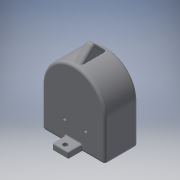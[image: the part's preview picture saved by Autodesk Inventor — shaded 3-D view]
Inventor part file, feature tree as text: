
AUTODESK INVENTOR PART (.ipt)
format: ipt  version: 2018 (Build 220112000, 112)  size: 283,648 bytes
history: native  units: in
note: dims shown in document units (in); Inventor stores cm internally (conversion verified against a paired STEP export)
features: extrude x7, fillet x7, sketch x6, reference x5, plane x1
ambient origin geometry x8: Origin, YZ Plane, XZ Plane, XY Plane, X Axis, Y Axis, Z Axis, Center Point
bodies: Solid1 (feature_tree)
feature tree (26):
  extrude  "Extrusion1"  Depth=0.197in
  extrude  "Extrusion2"  Depth=0.15in
  extrude  "Extrusion3"  Depth=0.4in TaperAngle=0.0deg
  extrude  "Extrusion4"  Depth=0.5in
  extrude  "Extrusion5"  Depth=0.4in TaperAngle=0.0deg
  plane  "Work Plane1"
  extrude  "Extrusion6"  Depth=0.1378in
  extrude  "Extrusion7"  Depth=0.4in TaperAngle=0.0deg
  fillet  "Fillet1"  Radius=0.5in
  fillet  "Fillet2"  Radius=1.9in
  fillet  "Fillet3"  [1 undecoded]
  fillet  "Fillet4"  Radius=0.1065in
  fillet  "Fillet5"  Radius=0.787in
  fillet  "Fillet6"  Radius=0.394in
  fillet  "Fillet7"  Radius=0.394in
  sketch  "Sketch1"  dims[d1=1.0in d2=0.0in d3=0.197in]
  reference  "Reference1"
  reference  "Reference2"
  sketch  "Sketch2"  dims[d4=0.4in d5=0.0in d6=0.15in]
  reference  "Reference3"
  sketch  "Sketch3"  dims[d7=0.1772in d8=0.4in d9=0.0in]
  sketch  "Sketch5"  dims[d10=0.25in d11=0.5in]
  sketch  "Sketch6"  dims[d12=0.197in d13=0.4in d14=0.0in]
  sketch  "Sketch7"  dims[d15=0.15in d16=0.1378in d17=0.4in d18=0.0in d19=0.5in d20=1.9in d21=-0.95in d22=0.1065in d23=0.787in d24=0.394in d25=0.394in d26=0.25in d27=0.0in d28=0.0394in d29=0.098in d30=0.0394in d31=0.098in d32=1.0in d33=0.0in d34=0.0394in d35=0.0394in d36=0.0787in d37=0.0787in d38=0.0787in d39=0.0787in d40=0.0394in]
  reference  "Reference4"
  reference  "Reference5"
note: 1 required parameter value undecoded (feature->parameter linkage not recoverable at this tier; creation-order binding heuristic only, values carry confidence <= 0.55)
